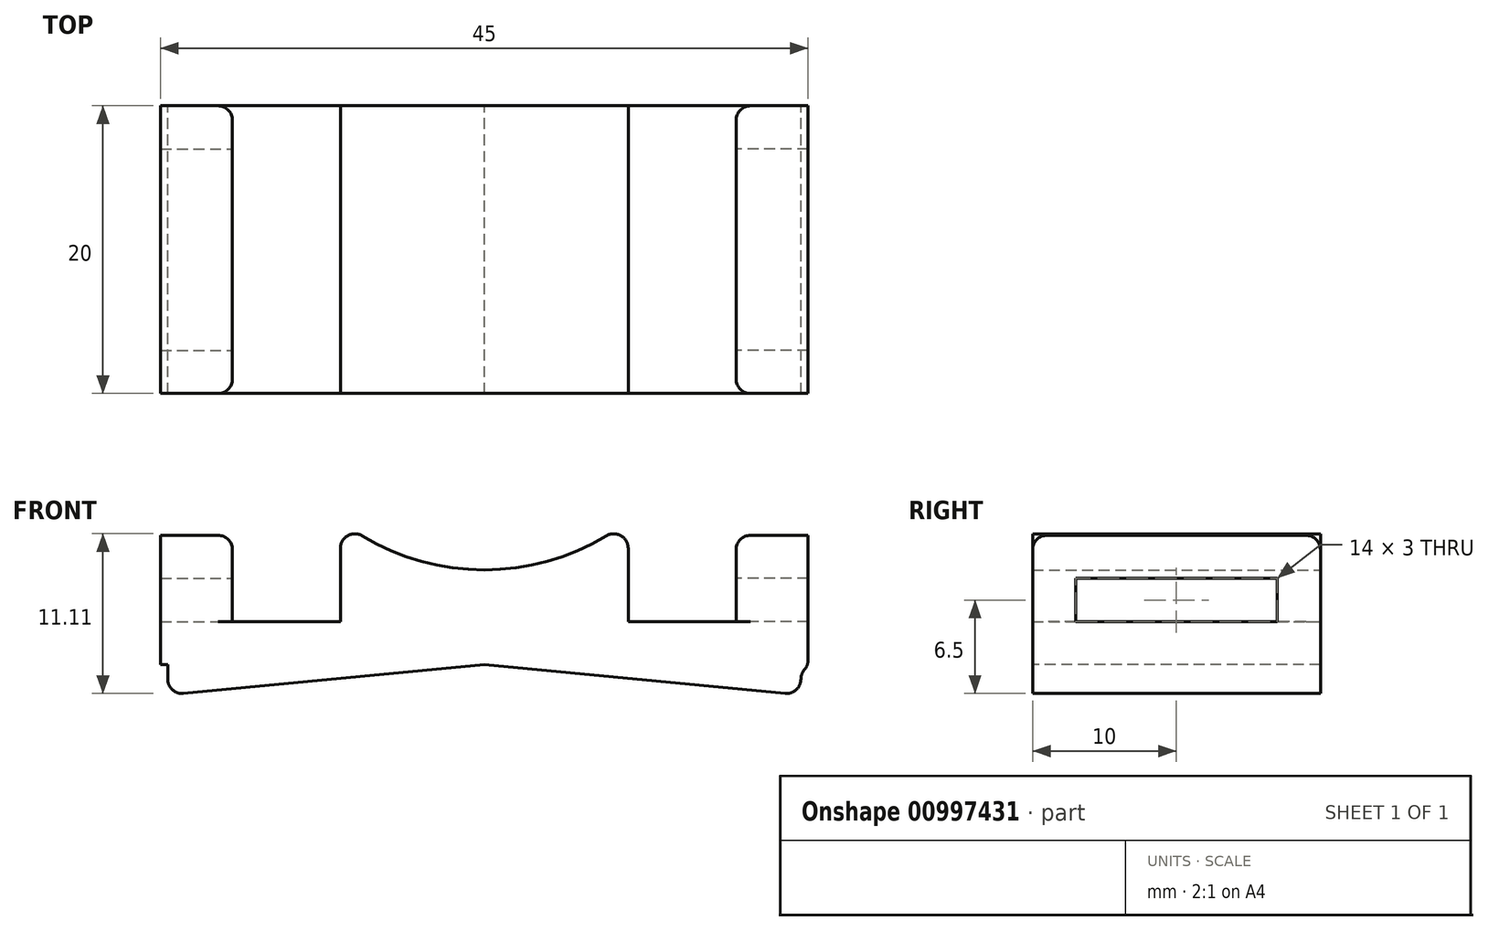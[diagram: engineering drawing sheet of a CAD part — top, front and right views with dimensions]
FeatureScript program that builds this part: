
annotation { "Feature Type Name" : "Feature", "Feature Type Description" : "" }
export const myFeature = defineFeature(function(context is Context, id is Id, definition is map)
    precondition{}
    {
        {
            var Q0;
            Q0=qCreatedBy(makeId("Top.planeOp"),FACE);
            var sketch = newSketch(context, id + "F0", { "sketchPlane" : qUnion([Q0])});
            skLineSegment(sketch, "E0.bottom", {"start": v(-25, 10) * mm, "end": v(25, 10) * mm});
            skLineSegment(sketch, "E0.top", {"start": v(-25, -10) * mm, "end": v(25, -10) * mm});
            skLineSegment(sketch, "E0.left", {"start": v(-25, 10) * mm, "end": v(-25, -10) * mm});
            skLineSegment(sketch, "E0.right", {"start": v(25, 10) * mm, "end": v(25, -10) * mm});
            skPoint(sketch, "E0.middle", {"position": v(0, 0) * mm});
            skSolve(sketch);
        }
        {
            var Q0;
            Q0=makeQuery(id+"F0.imprint","IMPRINT",FACE,{"disambiguationData":[TD([[makeQuery(id+"F0.imprint","IMPRINT",EDGE,{"derivedFrom":sQuery(id+"F0.wireOp",EDGE,"E0.bottom")}),-1.0]])]});
            extrude(context, id + "F1", {"entities" : qUnion([Q0]), "depth" : 3 * mm, "offsetDistance" : 25 * mm});
        }
        {
            var Q0;
            Q0=qCreatedBy(makeId("Front.planeOp"),FACE);
            var sketch = newSketch(context, id + "F2", { "sketchPlane" : qUnion([Q0])});
            skLineSegment(sketch, "E1.0.0", {"start": v(-25, 0) * mm, "end": v(25, 0) * mm});
            skLineSegment(sketch, "E1.0.1", {"start": v(25, 0) * mm, "end": v(25, 3) * mm});
            skLineSegment(sketch, "E1.0.2", {"start": v(25, 3) * mm, "end": v(-25, 3) * mm});
            skLineSegment(sketch, "E1.0.3", {"start": v(-25, 3) * mm, "end": v(-25, 0) * mm});
            skLineSegment(sketch, "E2", {"start": v(0, 0) * mm, "end": v(-22, -2.1) * mm});
            skLineSegment(sketch, "E3", {"start": v(-22, -2.1) * mm, "end": v(-22, 0) * mm});
            skLineSegment(sketch, "E4", {"start": v(0, 0) * mm, "end": v(22, -2.1) * mm});
            skLineSegment(sketch, "E5", {"start": v(22, 0) * mm, "end": v(22, -2.1) * mm});
            skSolve(sketch);
        }
        {
            var Q0;
            {var subQ2=sQuery(id+"F2.wireOp",EDGE,"E2");Q0=makeQuery(id+"F2.imprint","IMPRINT",FACE,{"disambiguationData":[TD([[makeQuery(id+"F2.imprint","IMPRINT",EDGE,{"derivedFrom":subQ2}),-1.0]])]});}
            var Q1;
            {var subQ2=sQuery(id+"F2.wireOp",EDGE,"E4");Q1=makeQuery(id+"F2.imprint","IMPRINT",FACE,{"disambiguationData":[TD([[makeQuery(id+"F2.imprint","IMPRINT",EDGE,{"derivedFrom":subQ2}),1.0]])]});}
            extrude(context, id + "F3", {"entities" : qUnion([Q0, Q1]), "operationType" : NewBodyOperationType.ADD, "depth" : 10 * mm, "offsetDistance" : 25 * mm});
        }
        {
            var Q0;
            Q0=makeQuery(id+"F3.opExtrude","CAP_FACE",FACE,{"disambiguationData":[OSD([sQuery(id+"F2.wireOp",EDGE,"E1.0.0"),sQuery(id+"F2.wireOp",EDGE,"E4"),sQuery(id+"F2.wireOp",EDGE,"E5")])],"isStart":true});
            var Q1;
            Q1=makeQuery(id+"F3.opExtrude","CAP_FACE",FACE,{"disambiguationData":[OSD([sQuery(id+"F2.wireOp",EDGE,"E1.0.0"),sQuery(id+"F2.wireOp",EDGE,"E2"),sQuery(id+"F2.wireOp",EDGE,"E3")])],"isStart":true});
            extrude(context, id + "F4", {"entities" : qUnion([Q0, Q1]), "operationType" : NewBodyOperationType.ADD, "depth" : 10 * mm, "offsetDistance" : 25 * mm});
        }
        {
            var Q0;
            Q0=makeQuery(id+"F1.opExtrude","CAP_FACE",FACE,{"disambiguationData":[OSD([sQuery(id+"F0.wireOp",EDGE,"E0.bottom"),sQuery(id+"F0.wireOp",EDGE,"E0.top"),sQuery(id+"F0.wireOp",EDGE,"E0.left"),sQuery(id+"F0.wireOp",EDGE,"E0.right")])],"isStart":false});
            var sketch = newSketch(context, id + "F5", { "sketchPlane" : qUnion([Q0])});
            skLineSegment(sketch, "E6.bottom", {"start": v(-25, 10) * mm, "end": v(-17.5, 10) * mm});
            skLineSegment(sketch, "E6.top", {"start": v(-25, -10) * mm, "end": v(-17.5, -10) * mm});
            skLineSegment(sketch, "E6.left", {"start": v(-25, 10) * mm, "end": v(-25, -10) * mm});
            skLineSegment(sketch, "E6.right", {"start": v(-17.5, 10) * mm, "end": v(-17.5, -10) * mm});
            skLineSegment(sketch, "E7.bottom", {"start": v(25, 10) * mm, "end": v(17.5, 10) * mm});
            skLineSegment(sketch, "E7.top", {"start": v(25, -10) * mm, "end": v(17.5, -10) * mm});
            skLineSegment(sketch, "E7.left", {"start": v(25, 10) * mm, "end": v(25, -10) * mm});
            skLineSegment(sketch, "E7.right", {"start": v(17.5, 10) * mm, "end": v(17.5, -10) * mm});
            skLineSegment(sketch, "E8", {"start": v(-22.5, 10) * mm, "end": v(-22.5, -10) * mm});
            skLineSegment(sketch, "E9", {"start": v(22.5, 10) * mm, "end": v(22.5, -10) * mm});
            skSolve(sketch);
        }
        {
            var Q0;
            Q0 = qSketchRegion(id + "F5", true);
            extrude(context, id + "F6", {"entities" : qUnion([Q0]), "operationType" : NewBodyOperationType.ADD, "depth" : 6 * mm, "offsetDistance" : 25 * mm});
        }
        {
            var Q0;
            Q0=makeQuery(id+"F6.opExtrude","SWEPT_FACE",FACE,{"disambiguationData":[OSD([sQuery(id+"F5.wireOp",EDGE,"E6.right")])]});
            var sketch = newSketch(context, id + "F7", { "sketchPlane" : qUnion([Q0])});
            skLineSegment(sketch, "E10.bottom", {"start": v(-7, 3) * mm, "end": v(7, 3) * mm});
            skLineSegment(sketch, "E10.top", {"start": v(-7, 6) * mm, "end": v(7, 6) * mm});
            skLineSegment(sketch, "E10.left", {"start": v(-7, 3) * mm, "end": v(-7, 6) * mm});
            skLineSegment(sketch, "E10.right", {"start": v(7, 3) * mm, "end": v(7, 6) * mm});
            skSolve(sketch);
        }
        {
            var Q0;
            Q0=makeQuery(id+"F7.imprint","IMPRINT",FACE,{"disambiguationData":[TD([[makeQuery(id+"F7.imprint","IMPRINT",EDGE,{"derivedFrom":sQuery(id+"F7.wireOp",EDGE,"E10.bottom")}),-1.0]])]});
            extrude(context, id + "F8", {"entities" : qUnion([Q0]), "operationType" : NewBodyOperationType.REMOVE, "oppositeDirection" : true, "depth" : 25 * mm, "offsetDistance" : 25 * mm});
        }
        {
            var Q0;
            Q0=makeQuery(id+"F6.opExtrude","SWEPT_FACE",FACE,{"disambiguationData":[OSD([sQuery(id+"F5.wireOp",EDGE,"E7.right")])]});
            var sketch = newSketch(context, id + "F9", { "sketchPlane" : qUnion([Q0])});
            skLineSegment(sketch, "E11.bottom", {"start": v(-7, 3) * mm, "end": v(7, 3) * mm});
            skLineSegment(sketch, "E11.top", {"start": v(-7, 6) * mm, "end": v(7, 6) * mm});
            skLineSegment(sketch, "E11.left", {"start": v(-7, 3) * mm, "end": v(-7, 6) * mm});
            skLineSegment(sketch, "E11.right", {"start": v(7, 3) * mm, "end": v(7, 6) * mm});
            skSolve(sketch);
        }
        {
            var Q0;
            Q0=makeQuery(id+"F9.imprint","IMPRINT",FACE,{"disambiguationData":[TD([[makeQuery(id+"F9.imprint","IMPRINT",EDGE,{"derivedFrom":sQuery(id+"F9.wireOp",EDGE,"E11.bottom")}),1.0]])]});
            extrude(context, id + "F10", {"entities" : qUnion([Q0]), "operationType" : NewBodyOperationType.REMOVE, "oppositeDirection" : true, "depth" : 25 * mm, "offsetDistance" : 25 * mm});
        }
        {
            var Q0;
            Q0=qCreatedBy(makeId("Front.planeOp"),FACE);
            var sketch = newSketch(context, id + "F11", { "sketchPlane" : qUnion([Q0])});
            skLineSegment(sketch, "E12.0", {"start": v(-17.5, 3) * mm, "end": v(17.5, 3) * mm});
            skLineSegment(sketch, "E13", {"start": v(-10, 3) * mm, "end": v(-10, 10) * mm});
            skLineSegment(sketch, "E14", {"start": v(10, 3) * mm, "end": v(10, 10) * mm});
            skArc(sketch, "E15", {"start": v(-10, 10) * mm, "mid": v(0, 6.6) * mm, "end": v(10, 10) * mm});
            skSolve(sketch);
        }
        {
            var Q0;
            {var subQ0=sQuery(id+"F11.wireOp",EDGE,"E13");Q0=makeQuery(id+"F11.imprint","IMPRINT",FACE,{"disambiguationData":[TD([[makeQuery(id+"F11.imprint","IMPRINT",EDGE,{"derivedFrom":subQ0}),-1.0]])]});}
            extrude(context, id + "F12", {"entities" : qUnion([Q0]), "operationType" : NewBodyOperationType.ADD, "depth" : 10 * mm, "offsetDistance" : 25 * mm});
        }
        {
            var Q0;
            Q0=makeQuery(id+"F12.opExtrude","CAP_FACE",FACE,{"disambiguationData":[OSD([sQuery(id+"F11.wireOp",EDGE,"E12.0"),sQuery(id+"F11.wireOp",EDGE,"E13"),sQuery(id+"F11.wireOp",EDGE,"E14"),sQuery(id+"F11.wireOp",EDGE,"E15")])],"isStart":true});
            extrude(context, id + "F13", {"entities" : qUnion([Q0]), "operationType" : NewBodyOperationType.ADD, "depth" : 10 * mm, "offsetDistance" : 25 * mm});
        }
        {
            var Q0;
            Q0=makeQuery(id+"F6.opExtrude","CAP_EDGE",EDGE,{"disambiguationData":[OSD([sQuery(id+"F5.wireOp",EDGE,"E6.right")])],"isStart":false});
            var Q1;
            Q1=makeQuery(id+"F1.opExtrude","CAP_EDGE",EDGE,{"disambiguationData":[OSD([sQuery(id+"F0.wireOp",EDGE,"E0.left")])],"isStart":true});
            var Q2;
            {var subQ0=sQuery(id+"F2.wireOp",EDGE,"E3");var subQ1=sQuery(id+"F2.wireOp",EDGE,"E1.0.0");Q2=makeQuery(id+"F4.boolean.opBoolean","MERGE",EDGE,{"derivedFrom":[makeQuery(id+"F3.opExtrude","SWEPT_EDGE",EDGE,{"disambiguationData":[OSD([subQ1,subQ0])]}),makeQuery(id+"F4.opExtrude","SWEPT_EDGE",EDGE,{"disambiguationData":[OSD([subQ1,subQ0])]})]});}
            var Q3;
            {var subQ0=sQuery(id+"F2.wireOp",EDGE,"E3");var subQ1=sQuery(id+"F2.wireOp",EDGE,"E2");Q3=makeQuery(id+"F4.boolean.opBoolean","MERGE",EDGE,{"derivedFrom":[makeQuery(id+"F3.opExtrude","SWEPT_EDGE",EDGE,{"disambiguationData":[OSD([subQ1,subQ0])]}),makeQuery(id+"F4.opExtrude","SWEPT_EDGE",EDGE,{"disambiguationData":[OSD([subQ1,subQ0])]})]});}
            var Q4;
            Q4=makeQuery(id+"F1.opExtrude","CAP_EDGE",EDGE,{"disambiguationData":[OSD([sQuery(id+"F0.wireOp",EDGE,"E0.right")])],"isStart":true});
            var Q5;
            {var subQ0=sQuery(id+"F2.wireOp",EDGE,"E5");var subQ1=sQuery(id+"F2.wireOp",EDGE,"E1.0.0");Q5=makeQuery(id+"F4.boolean.opBoolean","MERGE",EDGE,{"derivedFrom":[makeQuery(id+"F3.opExtrude","SWEPT_EDGE",EDGE,{"disambiguationData":[OSD([subQ1,subQ0])]}),makeQuery(id+"F4.opExtrude","SWEPT_EDGE",EDGE,{"disambiguationData":[OSD([subQ1,subQ0])]})]});}
            var Q6;
            {var subQ0=sQuery(id+"F2.wireOp",EDGE,"E5");var subQ1=sQuery(id+"F2.wireOp",EDGE,"E4");Q6=makeQuery(id+"F4.boolean.opBoolean","MERGE",EDGE,{"derivedFrom":[makeQuery(id+"F3.opExtrude","SWEPT_EDGE",EDGE,{"disambiguationData":[OSD([subQ1,subQ0])]}),makeQuery(id+"F4.opExtrude","SWEPT_EDGE",EDGE,{"disambiguationData":[OSD([subQ1,subQ0])]})]});}
            var Q7;
            Q7=makeQuery(id+"F6.opExtrude","CAP_EDGE",EDGE,{"disambiguationData":[OSD([sQuery(id+"F5.wireOp",EDGE,"E7.right")])],"isStart":false});
            var Q8;
            Q8=makeQuery(id+"F10.boolean.opBoolean","COPY",EDGE,{"derivedFrom":makeQuery(id+"F10.opExtrude","CAP_EDGE",EDGE,{"disambiguationData":[OSD([sQuery(id+"F9.wireOp",EDGE,"E11.top")])],"isStart":true})});
            var Q9;
            Q9=makeQuery(id+"F10.boolean.opBoolean","INTERSECT",EDGE,{"derivedFrom":[makeQuery(id+"F6.boolean.opBoolean","MERGE",FACE,{"derivedFrom":[makeQuery(id+"F1.opExtrude","SWEPT_FACE",FACE,{"disambiguationData":[OSD([sQuery(id+"F0.wireOp",EDGE,"E0.right")])]}),makeQuery(id+"F6.opExtrude","SWEPT_FACE",FACE,{"disambiguationData":[OSD([sQuery(id+"F5.wireOp",EDGE,"E7.left")])]})]}),makeQuery(id+"F10.opExtrude","SWEPT_FACE",FACE,{"disambiguationData":[OSD([sQuery(id+"F9.wireOp",EDGE,"E11.top")])]})]});
            var Q10;
            Q10=makeQuery(id+"F10.boolean.opBoolean","INTERSECT",EDGE,{"derivedFrom":[makeQuery(id+"F6.boolean.opBoolean","MERGE",FACE,{"derivedFrom":[makeQuery(id+"F1.opExtrude","SWEPT_FACE",FACE,{"disambiguationData":[OSD([sQuery(id+"F0.wireOp",EDGE,"E0.right")])]}),makeQuery(id+"F6.opExtrude","SWEPT_FACE",FACE,{"disambiguationData":[OSD([sQuery(id+"F5.wireOp",EDGE,"E7.left")])]})]}),makeQuery(id+"F10.opExtrude","SWEPT_FACE",FACE,{"disambiguationData":[OSD([sQuery(id+"F9.wireOp",EDGE,"E11.right")])]})]});
            var Q11;
            Q11=makeQuery(id+"F10.boolean.opBoolean","COPY",EDGE,{"derivedFrom":makeQuery(id+"F10.opExtrude","CAP_EDGE",EDGE,{"disambiguationData":[OSD([sQuery(id+"F9.wireOp",EDGE,"E11.right")])],"isStart":true})});
            var Q12;
            Q12=makeQuery(id+"F10.boolean.opBoolean","INTERSECT",EDGE,{"derivedFrom":[makeQuery(id+"F6.boolean.opBoolean","MERGE",FACE,{"derivedFrom":[makeQuery(id+"F1.opExtrude","SWEPT_FACE",FACE,{"disambiguationData":[OSD([sQuery(id+"F0.wireOp",EDGE,"E0.right")])]}),makeQuery(id+"F6.opExtrude","SWEPT_FACE",FACE,{"disambiguationData":[OSD([sQuery(id+"F5.wireOp",EDGE,"E7.left")])]})]}),makeQuery(id+"F10.opExtrude","SWEPT_FACE",FACE,{"disambiguationData":[OSD([sQuery(id+"F9.wireOp",EDGE,"E11.left")])]})]});
            var Q13;
            Q13=makeQuery(id+"F10.boolean.opBoolean","COPY",EDGE,{"derivedFrom":makeQuery(id+"F10.opExtrude","CAP_EDGE",EDGE,{"disambiguationData":[OSD([sQuery(id+"F9.wireOp",EDGE,"E11.left")])],"isStart":true})});
            var Q14;
            Q14=makeQuery(id+"F10.boolean.opBoolean","INTERSECT",EDGE,{"derivedFrom":[makeQuery(id+"F6.boolean.opBoolean","MERGE",FACE,{"derivedFrom":[makeQuery(id+"F1.opExtrude","SWEPT_FACE",FACE,{"disambiguationData":[OSD([sQuery(id+"F0.wireOp",EDGE,"E0.right")])]}),makeQuery(id+"F6.opExtrude","SWEPT_FACE",FACE,{"disambiguationData":[OSD([sQuery(id+"F5.wireOp",EDGE,"E7.left")])]})]}),makeQuery(id+"F10.opExtrude","SWEPT_FACE",FACE,{"disambiguationData":[OSD([sQuery(id+"F9.wireOp",EDGE,"E11.bottom")])]})]});
            var Q15;
            Q15=makeQuery(id+"F8.boolean.opBoolean","INTERSECT",EDGE,{"derivedFrom":[makeQuery(id+"F6.boolean.opBoolean","MERGE",FACE,{"derivedFrom":[makeQuery(id+"F1.opExtrude","SWEPT_FACE",FACE,{"disambiguationData":[OSD([sQuery(id+"F0.wireOp",EDGE,"E0.left")])]}),makeQuery(id+"F6.opExtrude","SWEPT_FACE",FACE,{"disambiguationData":[OSD([sQuery(id+"F5.wireOp",EDGE,"E6.left")])]})]}),makeQuery(id+"F8.opExtrude","SWEPT_FACE",FACE,{"disambiguationData":[OSD([sQuery(id+"F7.wireOp",EDGE,"E10.top")])]})]});
            var Q16;
            Q16=makeQuery(id+"F8.boolean.opBoolean","COPY",EDGE,{"derivedFrom":makeQuery(id+"F8.opExtrude","CAP_EDGE",EDGE,{"disambiguationData":[OSD([sQuery(id+"F7.wireOp",EDGE,"E10.left")])],"isStart":true})});
            var Q17;
            Q17=makeQuery(id+"F8.boolean.opBoolean","INTERSECT",EDGE,{"derivedFrom":[makeQuery(id+"F6.boolean.opBoolean","MERGE",FACE,{"derivedFrom":[makeQuery(id+"F1.opExtrude","SWEPT_FACE",FACE,{"disambiguationData":[OSD([sQuery(id+"F0.wireOp",EDGE,"E0.left")])]}),makeQuery(id+"F6.opExtrude","SWEPT_FACE",FACE,{"disambiguationData":[OSD([sQuery(id+"F5.wireOp",EDGE,"E6.left")])]})]}),makeQuery(id+"F8.opExtrude","SWEPT_FACE",FACE,{"disambiguationData":[OSD([sQuery(id+"F7.wireOp",EDGE,"E10.left")])]})]});
            var Q18;
            Q18=makeQuery(id+"F8.boolean.opBoolean","INTERSECT",EDGE,{"derivedFrom":[makeQuery(id+"F6.boolean.opBoolean","MERGE",FACE,{"derivedFrom":[makeQuery(id+"F1.opExtrude","SWEPT_FACE",FACE,{"disambiguationData":[OSD([sQuery(id+"F0.wireOp",EDGE,"E0.left")])]}),makeQuery(id+"F6.opExtrude","SWEPT_FACE",FACE,{"disambiguationData":[OSD([sQuery(id+"F5.wireOp",EDGE,"E6.left")])]})]}),makeQuery(id+"F8.opExtrude","SWEPT_FACE",FACE,{"disambiguationData":[OSD([sQuery(id+"F7.wireOp",EDGE,"E10.bottom")])]})]});
            var Q19;
            Q19=makeQuery(id+"F8.boolean.opBoolean","COPY",EDGE,{"derivedFrom":makeQuery(id+"F8.opExtrude","CAP_EDGE",EDGE,{"disambiguationData":[OSD([sQuery(id+"F7.wireOp",EDGE,"E10.top")])],"isStart":true})});
            var Q20;
            Q20=makeQuery(id+"F8.boolean.opBoolean","COPY",EDGE,{"derivedFrom":makeQuery(id+"F8.opExtrude","CAP_EDGE",EDGE,{"disambiguationData":[OSD([sQuery(id+"F7.wireOp",EDGE,"E10.right")])],"isStart":true})});
            fillet(context, id + "F14", {"entities" : qUnion([Q0, Q1, Q2, Q3, Q4, Q5, Q6, Q7, Q8, Q9, Q10, Q11, Q12, Q13, Q14, Q15, Q16, Q17, Q18, Q19, Q20]), "radius" : 1 * mm, "tangentPropagation" : true, "allowEdgeOverflow" : false});
        }
        {
            var Q0;
            {var subQ0=sQuery(id+"F11.wireOp",EDGE,"E15");var subQ1=sQuery(id+"F11.wireOp",EDGE,"E13");Q0=makeQuery(id+"F13.boolean.opBoolean","MERGE",EDGE,{"derivedFrom":[makeQuery(id+"F12.opExtrude","SWEPT_EDGE",EDGE,{"disambiguationData":[OSD([subQ1,subQ0])]}),makeQuery(id+"F13.opExtrude","SWEPT_EDGE",EDGE,{"disambiguationData":[OSD([subQ1,subQ0])]})]});}
            var Q1;
            {var subQ0=sQuery(id+"F11.wireOp",EDGE,"E15");var subQ1=sQuery(id+"F11.wireOp",EDGE,"E14");Q1=makeQuery(id+"F13.boolean.opBoolean","MERGE",EDGE,{"derivedFrom":[makeQuery(id+"F12.opExtrude","SWEPT_EDGE",EDGE,{"disambiguationData":[OSD([subQ1,subQ0])]}),makeQuery(id+"F13.opExtrude","SWEPT_EDGE",EDGE,{"disambiguationData":[OSD([subQ1,subQ0])]})]});}
            fillet(context, id + "F15", {"entities" : qUnion([Q0, Q1]), "radius" : 1 * mm, "tangentPropagation" : true, "allowEdgeOverflow" : false});
        }
        {
            var Q0;
            Q0=makeQuery(id+"F6.opExtrude","CAP_FACE",FACE,{"disambiguationData":[OSD([sQuery(id+"F5.wireOp",EDGE,"E6.bottom"),sQuery(id+"F5.wireOp",EDGE,"E6.top"),sQuery(id+"F5.wireOp",EDGE,"E6.left"),sQuery(id+"F5.wireOp",EDGE,"E6.right")])],"isStart":false});
            var sketch = newSketch(context, id + "F16", { "sketchPlane" : qUnion([Q0])});
            skLineSegment(sketch, "E16", {"start": v(-22.5, 10) * mm, "end": v(-22.5, -10) * mm});
            skSolve(sketch);
        }
        {
            var Q0;
            {var subQ0=sQuery(id+"F16.wireOp",EDGE,"E16");Q0=makeQuery(id+"F16.imprint","IMPRINT",FACE,{"disambiguationData":[TD([[makeQuery(id+"F16.imprint","IMPRINT",EDGE,{"derivedFrom":subQ0}),-1.0]])]});}
            extrude(context, id + "F17", {"entities" : qUnion([Q0]), "operationType" : NewBodyOperationType.REMOVE, "oppositeDirection" : true, "depth" : 25 * mm, "offsetDistance" : 25 * mm});
        }
        {
            var Q0;
            Q0=makeQuery(id+"F6.opExtrude","CAP_FACE",FACE,{"disambiguationData":[OSD([sQuery(id+"F5.wireOp",EDGE,"E7.bottom"),sQuery(id+"F5.wireOp",EDGE,"E7.top"),sQuery(id+"F5.wireOp",EDGE,"E7.left"),sQuery(id+"F5.wireOp",EDGE,"E7.right")])],"isStart":false});
            var sketch = newSketch(context, id + "F18", { "sketchPlane" : qUnion([Q0])});
            skLineSegment(sketch, "E17", {"start": v(22.5, 10) * mm, "end": v(22.5, -10) * mm});
            skSolve(sketch);
        }
        {
            var Q0;
            {var subQ0=sQuery(id+"F18.wireOp",EDGE,"E17");Q0=makeQuery(id+"F18.imprint","IMPRINT",FACE,{"disambiguationData":[TD([[makeQuery(id+"F18.imprint","IMPRINT",EDGE,{"derivedFrom":subQ0}),1.0]])]});}
            extrude(context, id + "F19", {"entities" : qUnion([Q0]), "operationType" : NewBodyOperationType.REMOVE, "oppositeDirection" : true, "depth" : 25 * mm, "offsetDistance" : 25 * mm});
        }
        {
            var Q0;
            Q0=makeQuery(id+"F17.boolean.opBoolean","INTERSECT",EDGE,{"derivedFrom":[makeQuery(id+"F14.opFillet","BLEND_FACE",FACE,{"disambiguationData":[OSD([sQuery(id+"F2.wireOp",EDGE,"E1.0.0"),sQuery(id+"F2.wireOp",EDGE,"E3")])]}),makeQuery(id+"F17.opExtrude","SWEPT_FACE",FACE,{"disambiguationData":[OSD([sQuery(id+"F16.wireOp",EDGE,"E16")])]})]});
            var Q1;
            Q1=makeQuery(id+"F19.boolean.opBoolean","INTERSECT",EDGE,{"derivedFrom":[makeQuery(id+"F14.opFillet","BLEND_FACE",FACE,{"disambiguationData":[OSD([sQuery(id+"F2.wireOp",EDGE,"E1.0.0"),sQuery(id+"F2.wireOp",EDGE,"E5")])]}),makeQuery(id+"F19.opExtrude","SWEPT_FACE",FACE,{"disambiguationData":[OSD([sQuery(id+"F18.wireOp",EDGE,"E17")])]})]});
            var Q2;
            Q2=makeQuery(id+"F19.boolean.opBoolean","COPY",EDGE,{"derivedFrom":makeQuery(id+"F19.opExtrude","CAP_EDGE",EDGE,{"disambiguationData":[OSD([sQuery(id+"F18.wireOp",EDGE,"E17")])],"isStart":true})});
            var Q3;
            Q3=makeQuery(id+"F6.opExtrude","CAP_EDGE",EDGE,{"disambiguationData":[OSD([sQuery(id+"F5.wireOp",EDGE,"E7.top")])],"isStart":false});
            var Q4;
            Q4=makeQuery(id+"F6.opExtrude","CAP_EDGE",EDGE,{"disambiguationData":[OSD([sQuery(id+"F5.wireOp",EDGE,"E7.bottom")])],"isStart":false});
            var Q5;
            Q5=makeQuery(id+"F6.opExtrude","CAP_EDGE",EDGE,{"disambiguationData":[OSD([sQuery(id+"F5.wireOp",EDGE,"E6.bottom")])],"isStart":false});
            var Q6;
            Q6=makeQuery(id+"F17.boolean.opBoolean","COPY",EDGE,{"derivedFrom":makeQuery(id+"F17.opExtrude","CAP_EDGE",EDGE,{"disambiguationData":[OSD([sQuery(id+"F16.wireOp",EDGE,"E16")])],"isStart":true})});
            var Q7;
            Q7=makeQuery(id+"F6.opExtrude","CAP_EDGE",EDGE,{"disambiguationData":[OSD([sQuery(id+"F5.wireOp",EDGE,"E6.top")])],"isStart":false});
            fillet(context, id + "F20", {"entities" : qUnion([Q0, Q1, Q2, Q3, Q4, Q5, Q6, Q7]), "radius" : 1 * mm, "tangentPropagation" : true, "allowEdgeOverflow" : false});
        }
    });
